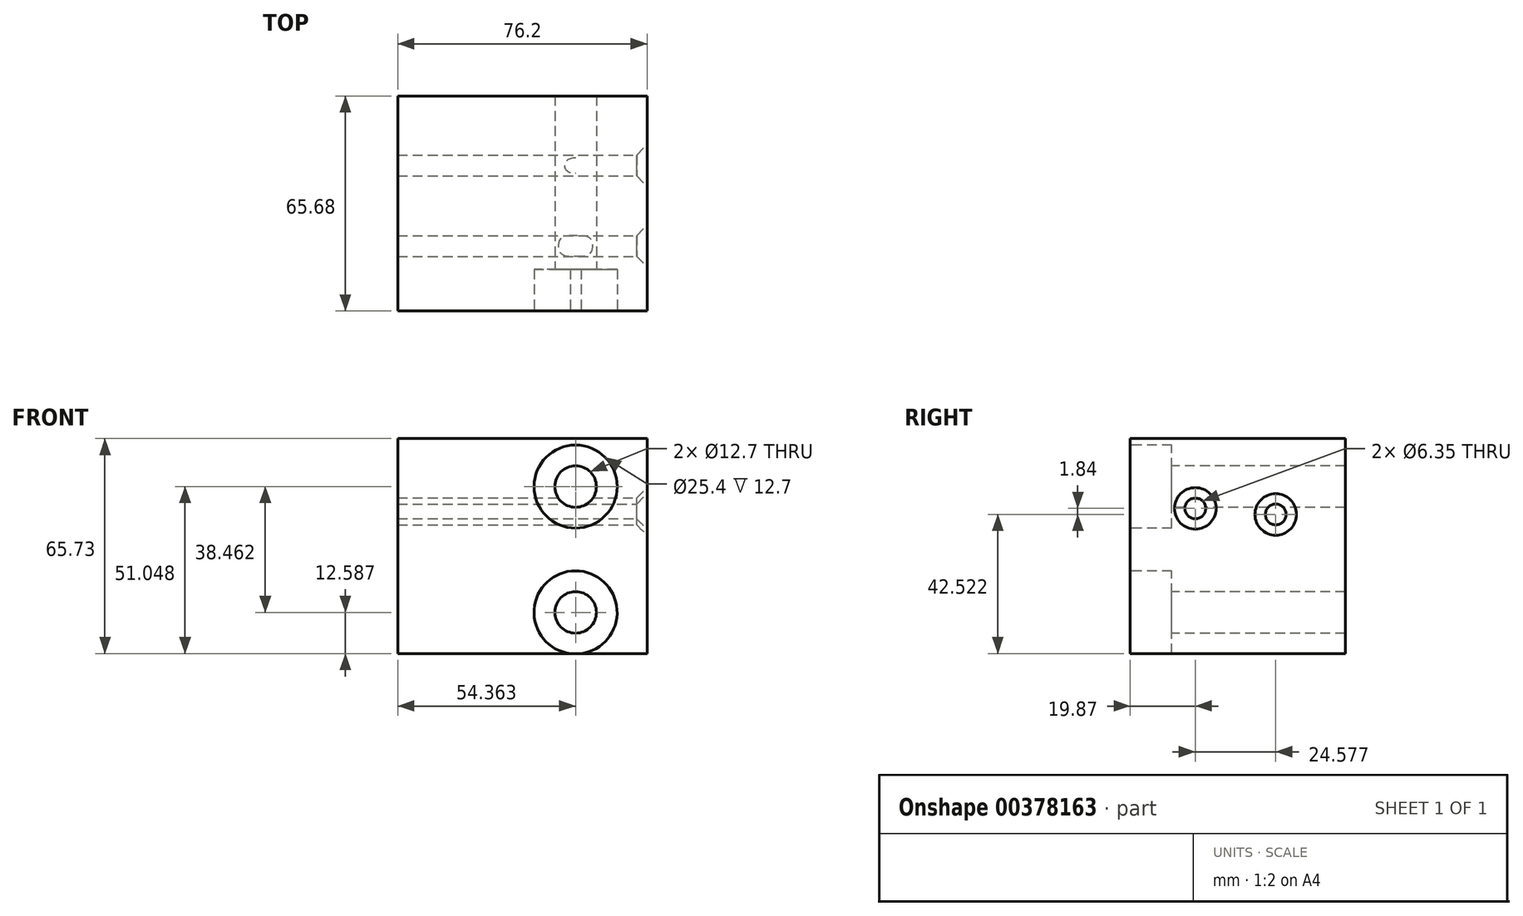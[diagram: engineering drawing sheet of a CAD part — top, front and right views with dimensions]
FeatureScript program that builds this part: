
annotation { "Feature Type Name" : "Feature", "Feature Type Description" : "" }
export const myFeature = defineFeature(function(context is Context, id is Id, definition is map)
    precondition{}
    {
        {
            var Q0;
            Q0=qCreatedBy(makeId("Right.planeOp"),FACE);
            var sketch = newSketch(context, id + "F0", { "sketchPlane" : qUnion([Q0])});
            skLineSegment(sketch, "E0.bottom", {"start": v(-26.36, 30.4) * mm, "end": v(39.32, 30.4) * mm});
            skLineSegment(sketch, "E0.top", {"start": v(-26.36, -35.33) * mm, "end": v(39.32, -35.33) * mm});
            skLineSegment(sketch, "E0.left", {"start": v(-26.36, 30.4) * mm, "end": v(-26.36, -35.33) * mm});
            skLineSegment(sketch, "E0.right", {"start": v(39.32, 30.4) * mm, "end": v(39.32, -35.33) * mm});
            skSolve(sketch);
        }
        {
            var Q0;
            Q0=makeQuery(id+"F0.imprint","IMPRINT",FACE,{"disambiguationData":[TD([[makeQuery(id+"F0.imprint","IMPRINT",EDGE,{"derivedFrom":sQuery(id+"F0.wireOp",EDGE,"E0.bottom")}),-1.0]])]});
            extrude(context, id + "F1", {"entities" : qUnion([Q0]), "depth" : 76.2 * mm});
        }
        {
            var Q0;
            Q0=makeQuery(id+"F1.opExtrude","CAP_FACE",FACE,{"disambiguationData":[OSD([sQuery(id+"F0.wireOp",EDGE,"E0.bottom"),sQuery(id+"F0.wireOp",EDGE,"E0.top"),sQuery(id+"F0.wireOp",EDGE,"E0.left"),sQuery(id+"F0.wireOp",EDGE,"E0.right")])],"isStart":false});
            var sketch = newSketch(context, id + "F2", { "sketchPlane" : qUnion([Q0])});
            skPoint(sketch, "E1", {"position": v(-6.5, 9.03) * mm});
            skPoint(sketch, "E2", {"position": v(18.09, 7.2) * mm});
            skPoint(sketch, "E3", {"position": v(-32.4, 68.82) * mm});
            skPoint(sketch, "E4", {"position": v(-51.62, 7.2) * mm});
            skPoint(sketch, "E5", {"position": v(-80.22, 60.99) * mm});
            skSolve(sketch);
        }
        {
            var Q0;
            Q0=sQuery(id+"F2.wireOp",VERTEX,"E1");
            var Q1;
            Q1=sQuery(id+"F2.wireOp",VERTEX,"E2");
            var Q2;
            Q2=makeQuery(id+"F1.opExtrude","SWEPT_BODY",BODY,{"disambiguationData":[OSD([sQuery(id+"F0.wireOp",EDGE,"E0.bottom"),sQuery(id+"F0.wireOp",EDGE,"E0.top"),sQuery(id+"F0.wireOp",EDGE,"E0.left"),sQuery(id+"F0.wireOp",EDGE,"E0.right")])]});
            hole(context, id + "F3", {"style" : HoleStyle.C_SINK, "endStyle" : HoleEndStyle.THROUGH, "holeDiameter" : 6.35 * mm, "cSinkDiameter" : 12.7 * mm, "cSinkAngle" : 90 * degree, "isTappedThrough" : true, "tappedDepth" : 12.7 * mm, "tapClearance" : 3, "locations" : qUnion([Q0, Q1]), "scope" : qUnion([Q2])});
        }
        {
            var Q0;
            Q0=makeQuery(id+"F1.opExtrude","SWEPT_FACE",FACE,{"disambiguationData":[OSD([sQuery(id+"F0.wireOp",EDGE,"E0.left")])]});
            var sketch = newSketch(context, id + "F4", { "sketchPlane" : qUnion([Q0])});
            skPoint(sketch, "E6", {"position": v(54.36, 15.72) * mm});
            skPoint(sketch, "E7", {"position": v(54.36, -22.74) * mm});
            skSolve(sketch);
        }
        {
            var Q0;
            Q0=sQuery(id+"F4.wireOp",VERTEX,"E6");
            var Q1;
            Q1=sQuery(id+"F4.wireOp",VERTEX,"E7");
            var Q2;
            Q2=makeQuery(id+"F1.opExtrude","SWEPT_BODY",BODY,{"disambiguationData":[OSD([sQuery(id+"F0.wireOp",EDGE,"E0.bottom"),sQuery(id+"F0.wireOp",EDGE,"E0.top"),sQuery(id+"F0.wireOp",EDGE,"E0.left"),sQuery(id+"F0.wireOp",EDGE,"E0.right")])]});
            hole(context, id + "F5", {"style" : HoleStyle.C_BORE, "endStyle" : HoleEndStyle.THROUGH, "holeDiameter" : 12.7 * mm, "cBoreDiameter" : 25.4 * mm, "cBoreDepth" : 12.7 * mm, "isTappedThrough" : true, "tappedDepth" : 12.7 * mm, "tapClearance" : 3, "locations" : qUnion([Q0, Q1]), "scope" : qUnion([Q2])});
        }
    });
